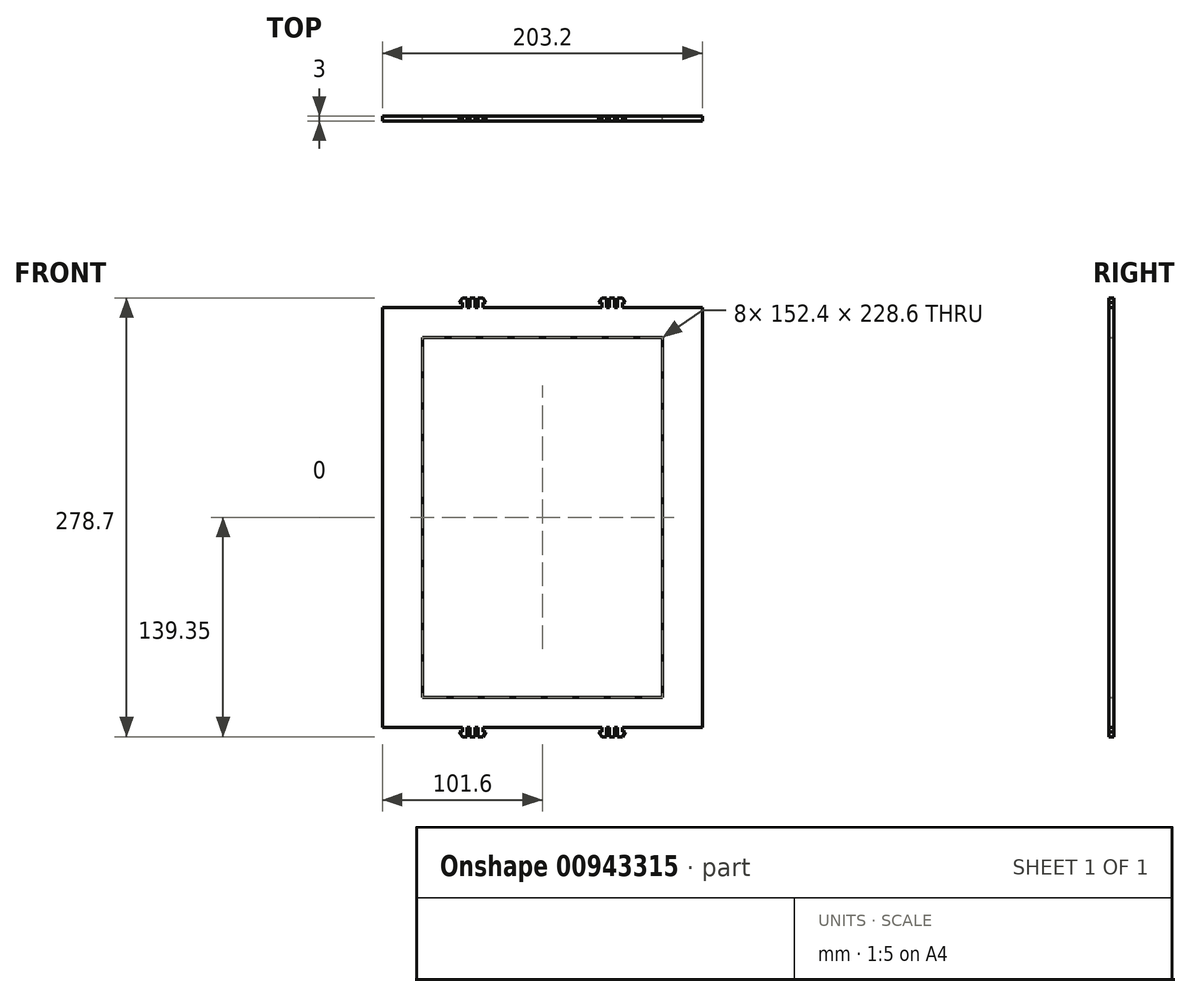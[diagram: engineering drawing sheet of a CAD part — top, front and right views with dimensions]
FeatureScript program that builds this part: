
annotation { "Feature Type Name" : "Feature", "Feature Type Description" : "" }
export const myFeature = defineFeature(function(context is Context, id is Id, definition is map)
    precondition{}
    {
        {
            var Q0;
            Q0=qCreatedBy(makeId("Front.planeOp"),FACE);
            var sketch = newSketch(context, id + "F0", { "sketchPlane" : qUnion([Q0])});
            skLineSegment(sketch, "E0.left", {"start": v(101.6, 133.35) * mm, "end": v(101.6, -133.35) * mm});
            skLineSegment(sketch, "E0.right", {"start": v(-101.6, 133.35) * mm, "end": v(-101.6, -133.35) * mm});
            skPoint(sketch, "E0.middle", {"position": v(0, 0) * mm});
            skLineSegment(sketch, "E1.bottom", {"start": v(76.2, 114.3) * mm, "end": v(-76.2, 114.3) * mm});
            skLineSegment(sketch, "E1.top", {"start": v(76.2, -114.3) * mm, "end": v(-76.2, -114.3) * mm});
            skLineSegment(sketch, "E1.left", {"start": v(76.2, 114.3) * mm, "end": v(76.2, -114.3) * mm});
            skLineSegment(sketch, "E1.right", {"start": v(-76.2, 114.3) * mm, "end": v(-76.2, -114.3) * mm});
            skLineSegment(sketch, "E2", {"start": v(-50.8, 133.35) * mm, "end": v(-50.8, 136.35) * mm});
            skLineSegment(sketch, "E3", {"start": v(-52.8, 136.35) * mm, "end": v(-50.8, 139.35) * mm});
            skLineSegment(sketch, "E4", {"start": v(-50.8, 139.35) * mm, "end": v(-47.8, 139.35) * mm});
            skLineSegment(sketch, "E5", {"start": v(-47.8, 139.35) * mm, "end": v(-47.8, 133.35) * mm});
            skLineSegment(sketch, "E6", {"start": v(-47.8, 133.35) * mm, "end": v(-45.8, 133.35) * mm});
            skLineSegment(sketch, "E7", {"start": v(-45.8, 133.35) * mm, "end": v(-45.8, 139.35) * mm});
            skLineSegment(sketch, "E8", {"start": v(-45.8, 139.35) * mm, "end": v(-42.8, 139.35) * mm});
            skLineSegment(sketch, "E9", {"start": v(-42.8, 139.35) * mm, "end": v(-42.8, 133.35) * mm});
            skLineSegment(sketch, "E10", {"start": v(-42.8, 133.35) * mm, "end": v(-40.8, 133.35) * mm});
            skLineSegment(sketch, "E11", {"start": v(-40.8, 133.35) * mm, "end": v(-40.8, 139.35) * mm});
            skLineSegment(sketch, "E12", {"start": v(-40.8, 139.35) * mm, "end": v(-37.8, 139.35) * mm});
            skLineSegment(sketch, "E13", {"start": v(-37.8, 139.35) * mm, "end": v(-35.8, 136.35) * mm});
            skLineSegment(sketch, "E14", {"start": v(-35.8, 136.35) * mm, "end": v(-37.8, 136.35) * mm});
            skLineSegment(sketch, "E15", {"start": v(-37.8, 136.35) * mm, "end": v(-37.8, 133.35) * mm});
            skLineSegment(sketch, "E16", {"start": v(-52.8, 136.35) * mm, "end": v(-50.8, 136.35) * mm});
            skLineSegment(sketch, "E17.trimOffspring", {"start": v(-50.8, 133.35) * mm, "end": v(-101.6, 133.35) * mm});
            skLineSegment(sketch, "E18", {"start": v(-37.8, 133.35) * mm, "end": v(101.6, 133.35) * mm});
            skLineSegment(sketch, "E19", {"start": v(37.8, 133.35) * mm, "end": v(37.8, 136.35) * mm});
            skLineSegment(sketch, "E20", {"start": v(35.8, 136.34) * mm, "end": v(37.8, 139.34) * mm});
            skLineSegment(sketch, "E21", {"start": v(37.8, 139.34) * mm, "end": v(40.8, 139.35) * mm});
            skLineSegment(sketch, "E22", {"start": v(40.8, 139.35) * mm, "end": v(40.8, 133.35) * mm});
            skLineSegment(sketch, "E23", {"start": v(40.8, 133.35) * mm, "end": v(42.8, 133.35) * mm});
            skLineSegment(sketch, "E24", {"start": v(42.8, 133.35) * mm, "end": v(42.8, 139.35) * mm});
            skLineSegment(sketch, "E25", {"start": v(42.8, 139.35) * mm, "end": v(45.8, 139.35) * mm});
            skLineSegment(sketch, "E26", {"start": v(45.8, 139.35) * mm, "end": v(45.8, 133.35) * mm});
            skLineSegment(sketch, "E27", {"start": v(45.8, 133.35) * mm, "end": v(47.8, 133.35) * mm});
            skLineSegment(sketch, "E28", {"start": v(47.8, 133.35) * mm, "end": v(47.8, 139.35) * mm});
            skLineSegment(sketch, "E29", {"start": v(47.8, 139.35) * mm, "end": v(50.8, 139.35) * mm});
            skLineSegment(sketch, "E30", {"start": v(50.8, 139.35) * mm, "end": v(52.8, 136.35) * mm});
            skLineSegment(sketch, "E31", {"start": v(52.8, 136.35) * mm, "end": v(50.8, 136.35) * mm});
            skLineSegment(sketch, "E32", {"start": v(50.8, 136.35) * mm, "end": v(50.8, 133.35) * mm});
            skLineSegment(sketch, "E33", {"start": v(35.8, 136.34) * mm, "end": v(37.8, 136.35) * mm});
            skLineSegment(sketch, "E34.MirrorCS", {"start": v(-37.8, -136.35) * mm, "end": v(-37.8, -133.35) * mm});
            skLineSegment(sketch, "E35.MirrorCS", {"start": v(-35.8, -136.35) * mm, "end": v(-37.8, -136.35) * mm});
            skLineSegment(sketch, "E36.MirrorCS", {"start": v(-37.8, -139.35) * mm, "end": v(-35.8, -136.35) * mm});
            skLineSegment(sketch, "E37.MirrorCS", {"start": v(-52.8, -136.35) * mm, "end": v(-50.8, -136.35) * mm});
            skLineSegment(sketch, "E38.MirrorCS", {"start": v(-50.8, -133.35) * mm, "end": v(-50.8, -136.35) * mm});
            skLineSegment(sketch, "E39.MirrorCS", {"start": v(-52.8, -136.35) * mm, "end": v(-50.8, -139.35) * mm});
            skLineSegment(sketch, "E40.MirrorCS", {"start": v(-50.8, -139.35) * mm, "end": v(-47.8, -139.35) * mm});
            skLineSegment(sketch, "E41.MirrorCS", {"start": v(-42.8, -139.35) * mm, "end": v(-42.8, -133.35) * mm});
            skLineSegment(sketch, "E42.MirrorCS", {"start": v(-40.8, -133.35) * mm, "end": v(-40.8, -139.35) * mm});
            skLineSegment(sketch, "E43.MirrorCS", {"start": v(-47.8, -139.35) * mm, "end": v(-47.8, -133.35) * mm});
            skLineSegment(sketch, "E44.MirrorCS", {"start": v(-45.8, -133.35) * mm, "end": v(-45.8, -139.35) * mm});
            skLineSegment(sketch, "E45.MirrorCS", {"start": v(-40.8, -139.35) * mm, "end": v(-37.8, -139.35) * mm});
            skLineSegment(sketch, "E46.MirrorCS", {"start": v(-45.8, -139.35) * mm, "end": v(-42.8, -139.35) * mm});
            skLineSegment(sketch, "E47", {"start": v(-47.8, -133.35) * mm, "end": v(-45.8, -133.35) * mm});
            skLineSegment(sketch, "E48", {"start": v(-42.8, -133.35) * mm, "end": v(-40.8, -133.35) * mm});
            skLineSegment(sketch, "E49.trimOffspring", {"start": v(-50.8, -133.35) * mm, "end": v(-101.6, -133.35) * mm});
            skLineSegment(sketch, "E50.trimOffspring", {"start": v(-45.8, -133.35) * mm, "end": v(-47.8, -133.35) * mm});
            skLineSegment(sketch, "E51.trimOffspring", {"start": v(-40.8, -133.35) * mm, "end": v(-42.8, -133.35) * mm});
            skLineSegment(sketch, "E52", {"start": v(-37.8, -133.35) * mm, "end": v(37.8, -133.35) * mm});
            skLineSegment(sketch, "E53", {"start": v(101.6, -133.35) * mm, "end": v(50.8, -133.35) * mm});
            skLineSegment(sketch, "E54.MirrorCS", {"start": v(50.8, -136.35) * mm, "end": v(50.8, -133.35) * mm});
            skLineSegment(sketch, "E55.MirrorCS", {"start": v(52.8, -136.35) * mm, "end": v(50.8, -136.35) * mm});
            skLineSegment(sketch, "E56.MirrorCS", {"start": v(50.8, -139.35) * mm, "end": v(52.8, -136.35) * mm});
            skLineSegment(sketch, "E57.MirrorCS", {"start": v(35.8, -136.35) * mm, "end": v(37.8, -136.35) * mm});
            skLineSegment(sketch, "E58.MirrorCS", {"start": v(37.8, -133.35) * mm, "end": v(37.8, -136.35) * mm});
            skLineSegment(sketch, "E59.MirrorCS", {"start": v(35.8, -136.35) * mm, "end": v(37.8, -139.35) * mm});
            skLineSegment(sketch, "E60.MirrorCS", {"start": v(37.8, -139.35) * mm, "end": v(40.8, -139.35) * mm});
            skLineSegment(sketch, "E61.MirrorCS", {"start": v(45.8, -139.35) * mm, "end": v(45.8, -133.35) * mm});
            skLineSegment(sketch, "E62.MirrorCS", {"start": v(47.8, -133.35) * mm, "end": v(47.8, -139.35) * mm});
            skLineSegment(sketch, "E63.MirrorCS", {"start": v(40.8, -139.35) * mm, "end": v(40.8, -133.35) * mm});
            skLineSegment(sketch, "E64.MirrorCS", {"start": v(42.8, -133.35) * mm, "end": v(42.8, -139.35) * mm});
            skLineSegment(sketch, "E65.MirrorCS", {"start": v(47.8, -139.35) * mm, "end": v(50.8, -139.35) * mm});
            skLineSegment(sketch, "E66.MirrorCS", {"start": v(42.8, -139.35) * mm, "end": v(45.8, -139.35) * mm});
            skLineSegment(sketch, "E67", {"start": v(40.8, -133.35) * mm, "end": v(42.8, -133.35) * mm});
            skLineSegment(sketch, "E68", {"start": v(45.8, -133.35) * mm, "end": v(47.8, -133.35) * mm});
            skLineSegment(sketch, "E69.trimOffspring", {"start": v(50.8, -133.35) * mm, "end": v(101.6, -133.35) * mm});
            skSolve(sketch);
        }
        {
            var Q0;
            Q0 = qSketchRegion(id + "F0", true);
            extrude(context, id + "F1", {"entities" : qUnion([Q0]), "depth" : 3 * mm, "offsetDistance" : 25.4 * mm});
        }
    });
